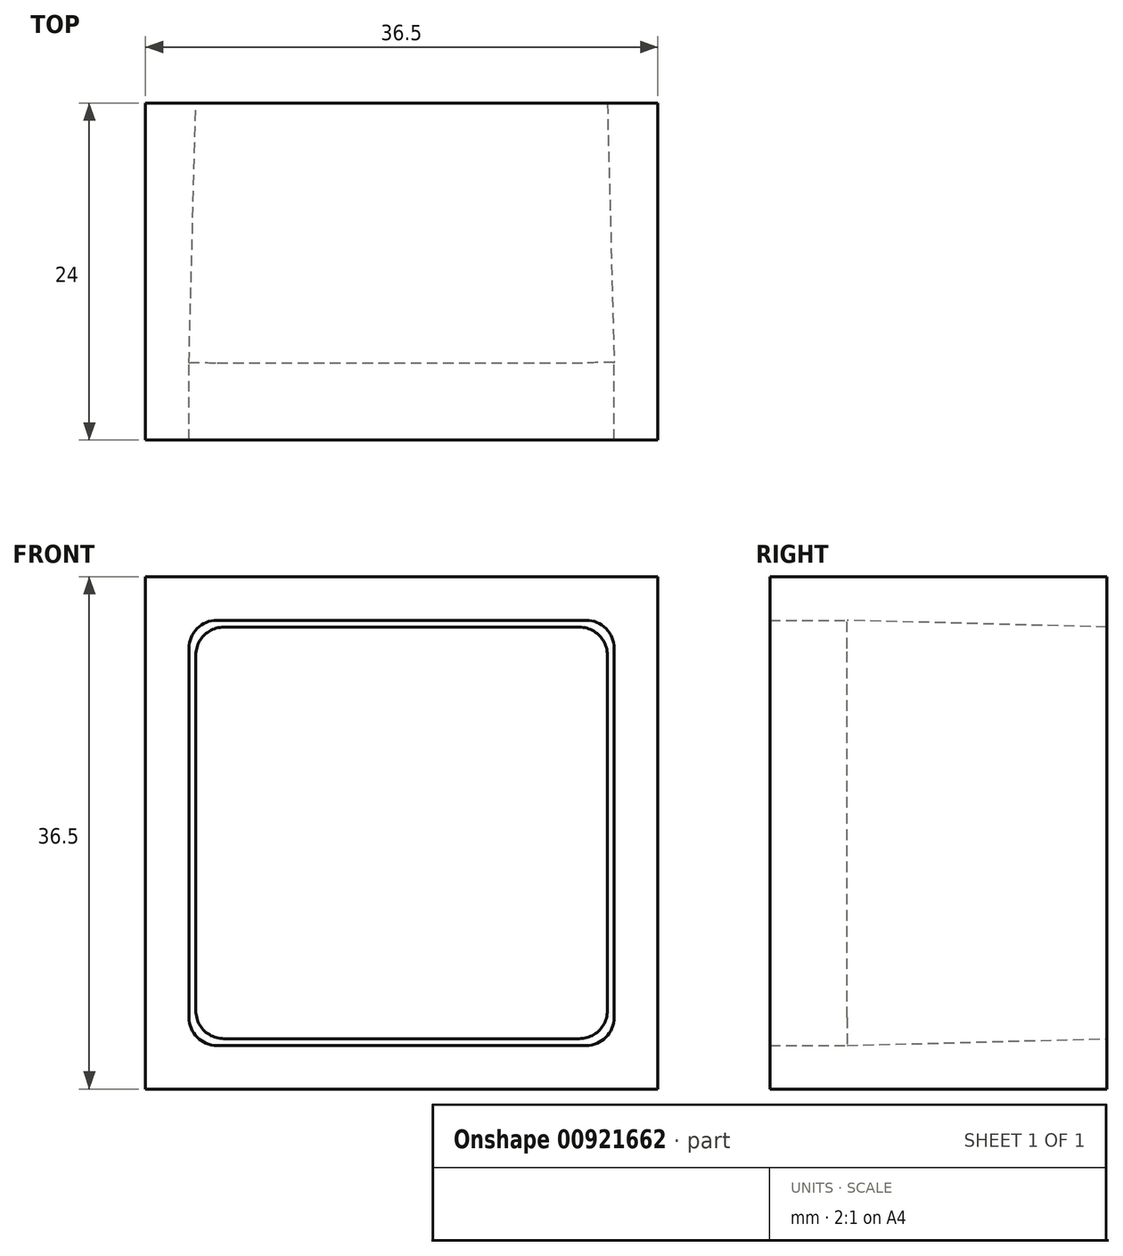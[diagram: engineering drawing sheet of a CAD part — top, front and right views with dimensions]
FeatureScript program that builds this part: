
annotation { "Feature Type Name" : "Feature", "Feature Type Description" : "" }
export const myFeature = defineFeature(function(context is Context, id is Id, definition is map)
    precondition{}
    {
        {
            var Q0;
            Q0=qCreatedBy(makeId("Front.planeOp"),FACE);
            var sketch = newSketch(context, id + "F0", { "sketchPlane" : qUnion([Q0])});
            skLineSegment(sketch, "E0.bottom", {"start": v(-36.5, 36.5) * mm, "end": v(0, 36.5) * mm});
            skLineSegment(sketch, "E0.top", {"start": v(-36.5, 0) * mm, "end": v(0, 0) * mm});
            skLineSegment(sketch, "E0.left", {"start": v(-36.5, 36.5) * mm, "end": v(-36.5, 0) * mm});
            skLineSegment(sketch, "E0.right", {"start": v(0, 36.5) * mm, "end": v(0, 0) * mm});
            skSolve(sketch);
        }
        {
            var Q0;
            Q0=qCreatedBy(makeId("Front.planeOp"),FACE);
            cPlane(context, id + "F1", {"entities" : qUnion([Q0]), "cplaneType" : CPlaneType.OFFSET, "offset" : 5.5 * mm, "oppositeDirection" : true, "width" : 150 * mm, "height" : 150 * mm});
        }
        {
            var Q0;
            Q0=qCreatedBy(id+"F1.planeOp",FACE);
            var sketch = newSketch(context, id + "F2", { "sketchPlane" : qUnion([Q0])});
            skLineSegment(sketch, "E1.bottom", {"start": v(-33.4, 33.4) * mm, "end": v(-3.1, 33.4) * mm});
            skLineSegment(sketch, "E1.top", {"start": v(-33.4, 3.1) * mm, "end": v(-3.1, 3.1) * mm});
            skLineSegment(sketch, "E1.left", {"start": v(-33.4, 33.4) * mm, "end": v(-33.4, 3.1) * mm});
            skLineSegment(sketch, "E1.right", {"start": v(-3.1, 33.4) * mm, "end": v(-3.1, 3.1) * mm});
            skSolve(sketch);
        }
        {
            var Q0;
            Q0=qCreatedBy(id+"F1.planeOp",FACE);
            cPlane(context, id + "F3", {"entities" : qUnion([Q0]), "cplaneType" : CPlaneType.OFFSET, "offset" : 19 * mm, "oppositeDirection" : true, "width" : 150 * mm, "height" : 150 * mm});
        }
        {
            var Q0;
            Q0=qCreatedBy(id+"F3.planeOp",FACE);
            var sketch = newSketch(context, id + "F4", { "sketchPlane" : qUnion([Q0])});
            skLineSegment(sketch, "E2.bottom", {"start": v(-36.5, 36.5) * mm, "end": v(0, 36.5) * mm});
            skLineSegment(sketch, "E2.top", {"start": v(-36.5, 0) * mm, "end": v(0, 0) * mm});
            skLineSegment(sketch, "E2.left", {"start": v(-36.5, 36.5) * mm, "end": v(-36.5, 0) * mm});
            skLineSegment(sketch, "E2.right", {"start": v(0, 36.5) * mm, "end": v(0, 0) * mm});
            skLineSegment(sketch, "E3.bottom", {"start": v(-32.9, 32.9) * mm, "end": v(-3.6, 32.9) * mm});
            skLineSegment(sketch, "E3.top", {"start": v(-32.9, 3.6) * mm, "end": v(-3.6, 3.6) * mm});
            skLineSegment(sketch, "E3.left", {"start": v(-32.9, 32.9) * mm, "end": v(-32.9, 3.6) * mm});
            skLineSegment(sketch, "E3.right", {"start": v(-3.6, 32.9) * mm, "end": v(-3.6, 3.6) * mm});
            skSolve(sketch);
        }
        {
            var Q0;
            Q0 = qSketchRegion(id + "F0", true);
            extrude(context, id + "F5", {"entities" : qUnion([Q0]), "oppositeDirection" : true, "depth" : 24 * mm, "offsetDistance" : 25 * mm});
        }
        {
            var Q0;
            Q0=makeQuery(id+"F4.imprint","IMPRINT",FACE,{"disambiguationData":[TD([[makeQuery(id+"F4.imprint","IMPRINT",EDGE,{"derivedFrom":sQuery(id+"F4.wireOp",EDGE,"E3.bottom")}),-1.0]])]});
            extrude(context, id + "F6", {"entities" : qUnion([Q0]), "operationType" : NewBodyOperationType.REMOVE, "depth" : 19 * mm, "offsetDistance" : 25 * mm, "hasDraft" : true, "draftAngle" : 1.5 * degree});
        }
        {
            var Q0;
            Q0 = qSketchRegion(id + "F2", true);
            extrude(context, id + "F7", {"entities" : qUnion([Q0]), "operationType" : NewBodyOperationType.REMOVE, "endBound" : BoundingType.THROUGH_ALL, "depth" : 5.5 * mm, "offsetDistance" : 25 * mm});
        }
        {
            var Q0;
            Q0=makeQuery(id+"F6.boolean.opBoolean","COPY",EDGE,{"derivedFrom":makeQuery(id+"F6.opExtrude","SWEPT_EDGE",EDGE,{"disambiguationData":[OSD([sQuery(id+"F4.wireOp",EDGE,"E3.bottom"),sQuery(id+"F4.wireOp",EDGE,"E3.right")])]})});
            var Q1;
            Q1=makeQuery(id+"F7.boolean.opBoolean","COPY",EDGE,{"derivedFrom":makeQuery(id+"F7.opExtrude","SWEPT_EDGE",EDGE,{"disambiguationData":[OSD([sQuery(id+"F2.wireOp",EDGE,"E1.bottom"),sQuery(id+"F2.wireOp",EDGE,"E1.right")])]})});
            var Q2;
            Q2=makeQuery(id+"F6.boolean.opBoolean","COPY",EDGE,{"derivedFrom":makeQuery(id+"F6.opExtrude","SWEPT_EDGE",EDGE,{"disambiguationData":[OSD([sQuery(id+"F4.wireOp",EDGE,"E3.top"),sQuery(id+"F4.wireOp",EDGE,"E3.left")])]})});
            var Q3;
            Q3=makeQuery(id+"F7.boolean.opBoolean","COPY",EDGE,{"derivedFrom":makeQuery(id+"F7.opExtrude","SWEPT_EDGE",EDGE,{"disambiguationData":[OSD([sQuery(id+"F2.wireOp",EDGE,"E1.top"),sQuery(id+"F2.wireOp",EDGE,"E1.left")])]})});
            var Q4;
            Q4=makeQuery(id+"F6.boolean.opBoolean","COPY",EDGE,{"derivedFrom":makeQuery(id+"F6.opExtrude","SWEPT_EDGE",EDGE,{"disambiguationData":[OSD([sQuery(id+"F4.wireOp",EDGE,"E3.bottom"),sQuery(id+"F4.wireOp",EDGE,"E3.left")])]})});
            var Q5;
            Q5=makeQuery(id+"F7.boolean.opBoolean","COPY",EDGE,{"derivedFrom":makeQuery(id+"F7.opExtrude","SWEPT_EDGE",EDGE,{"disambiguationData":[OSD([sQuery(id+"F2.wireOp",EDGE,"E1.bottom"),sQuery(id+"F2.wireOp",EDGE,"E1.left")])]})});
            var Q6;
            Q6=makeQuery(id+"F6.boolean.opBoolean","COPY",EDGE,{"derivedFrom":makeQuery(id+"F6.opExtrude","SWEPT_EDGE",EDGE,{"disambiguationData":[OSD([sQuery(id+"F4.wireOp",EDGE,"E3.top"),sQuery(id+"F4.wireOp",EDGE,"E3.right")])]})});
            var Q7;
            Q7=makeQuery(id+"F7.boolean.opBoolean","COPY",EDGE,{"derivedFrom":makeQuery(id+"F7.opExtrude","SWEPT_EDGE",EDGE,{"disambiguationData":[OSD([sQuery(id+"F2.wireOp",EDGE,"E1.top"),sQuery(id+"F2.wireOp",EDGE,"E1.right")])]})});
            fillet(context, id + "F8", {"entities" : qUnion([Q0, Q1, Q2, Q3, Q4, Q5, Q6, Q7]), "radius" : 2 * mm, "tangentPropagation" : true, "allowEdgeOverflow" : false});
        }
    });
